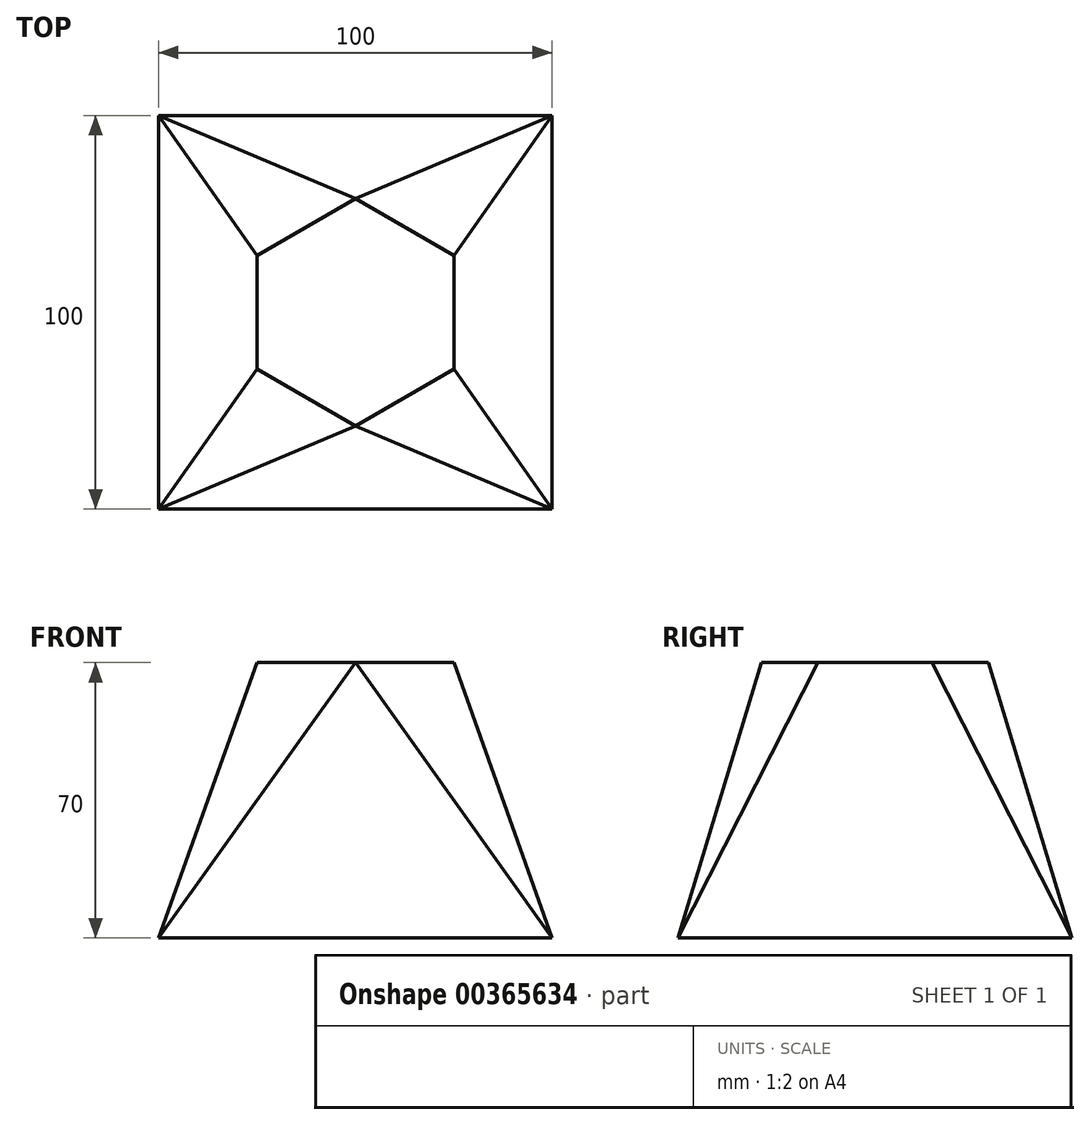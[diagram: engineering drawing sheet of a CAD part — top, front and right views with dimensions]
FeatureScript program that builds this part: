
annotation { "Feature Type Name" : "Feature", "Feature Type Description" : "" }
export const myFeature = defineFeature(function(context is Context, id is Id, definition is map)
    precondition{}
    {
        {
            var Q0;
            Q0=qCreatedBy(makeId("Top.planeOp"),FACE);
            var sketch = newSketch(context, id + "F0", { "sketchPlane" : qUnion([Q0])});
            skLineSegment(sketch, "E0.bottom", {"start": v(50, -50) * mm, "end": v(-50, -50) * mm});
            skLineSegment(sketch, "E0.top", {"start": v(50, 50) * mm, "end": v(-50, 50) * mm});
            skLineSegment(sketch, "E0.left", {"start": v(50, -50) * mm, "end": v(50, 50) * mm});
            skLineSegment(sketch, "E0.right", {"start": v(-50, -50) * mm, "end": v(-50, 50) * mm});
            skPoint(sketch, "E0.middle", {"position": v(0, 0) * mm});
            skSolve(sketch);
        }
        {
            var Q0;
            Q0=qCreatedBy(makeId("Top.planeOp"),FACE);
            cPlane(context, id + "F1", {"entities" : qUnion([Q0]), "cplaneType" : CPlaneType.OFFSET, "offset" : 70 * mm, "width" : 150 * mm, "height" : 150 * mm});
        }
        {
            var Q0;
            Q0=qCreatedBy(id+"F1.planeOp",FACE);
            var sketch = newSketch(context, id + "F2", { "sketchPlane" : qUnion([Q0])});
            skCircle(sketch, "E1.cCircle", {"center": v(0, 0) * mm, "radius": 25 * mm, "construction": true});
            skLineSegment(sketch, "E1.0", {"start": v(-25, -14.43) * mm, "end": v(-25, 14.43) * mm});
            skLineSegment(sketch, "E1.1", {"start": v(-25, 14.43) * mm, "end": v(0, 28.87) * mm});
            skLineSegment(sketch, "E1.2", {"start": v(0, 28.87) * mm, "end": v(25, 14.43) * mm});
            skLineSegment(sketch, "E1.3", {"start": v(25, 14.43) * mm, "end": v(25, -14.43) * mm});
            skLineSegment(sketch, "E1.4", {"start": v(25, -14.43) * mm, "end": v(0, -28.87) * mm});
            skLineSegment(sketch, "E1.5", {"start": v(0, -28.87) * mm, "end": v(-25, -14.43) * mm});
            skPoint(sketch, "E1.0.midPoint", {"position": v(-25, 0) * mm});
            skLineSegment(sketch, "E2", {"start": v(25, 14.43) * mm, "end": v(-25, 14.43) * mm});
            skLineSegment(sketch, "E3", {"start": v(25, -14.43) * mm, "end": v(-25, -14.43) * mm});
            skSolve(sketch);
        }
        {
            var Q0;
            Q0=makeQuery(id+"F2.imprint","IMPRINT",FACE,{"disambiguationData":[TD([[makeQuery(id+"F2.imprint","IMPRINT",EDGE,{"derivedFrom":sQuery(id+"F2.wireOp",EDGE,"E1.0")}),-1.0]])]});
            var Q1;
            Q1=makeQuery(id+"F0.imprint","IMPRINT",FACE,{"disambiguationData":[TD([[makeQuery(id+"F0.imprint","IMPRINT",EDGE,{"derivedFrom":sQuery(id+"F0.wireOp",EDGE,"E0.bottom")}),-1.0]])]});
            loft(context, id + "F3", {"sheetProfilesArray" : [{ "sheetProfileEntities" : qUnion([Q0]) }, { "sheetProfileEntities" : qUnion([Q1]) }]});
        }
        {
            var Q1;
            Q1=makeQuery(id+"F2.imprint","IMPRINT",FACE,{"disambiguationData":[TD([[makeQuery(id+"F2.imprint","IMPRINT",EDGE,{"derivedFrom":sQuery(id+"F2.wireOp",EDGE,"E1.1")}),-1.0]])]});
            var Q2;
            Q2=makeQuery(id+"F3.opLoft","MID_CAP_VERTEX",VERTEX,{"disambiguationData":[OSD([sQuery(id+"F0.wireOp",EDGE,"E0.top"),sQuery(id+"F0.wireOp",EDGE,"E0.left")])],"capPos":1.0});
            loft(context, id + "F4", {"operationType" : NewBodyOperationType.ADD, "sheetProfilesArray" : [{ "sheetProfileEntities" : qUnion([Q1]) }, { "sheetProfileEntities" : qUnion([Q2]) }]});
        }
        {
            var Q1;
            Q1=makeQuery(id+"F2.imprint","IMPRINT",FACE,{"disambiguationData":[TD([[makeQuery(id+"F2.imprint","IMPRINT",EDGE,{"derivedFrom":sQuery(id+"F2.wireOp",EDGE,"E1.1")}),-1.0]])]});
            var Q2;
            Q2=makeQuery(id+"F3.opLoft","MID_CAP_VERTEX",VERTEX,{"disambiguationData":[OSD([sQuery(id+"F0.wireOp",EDGE,"E0.top"),sQuery(id+"F0.wireOp",EDGE,"E0.right")])],"capPos":1.0});
            loft(context, id + "F5", {"operationType" : NewBodyOperationType.ADD, "sheetProfilesArray" : [{ "sheetProfileEntities" : qUnion([Q1]) }, { "sheetProfileEntities" : qUnion([Q2]) }]});
        }
        {
            var Q1;
            Q1=makeQuery(id+"F2.imprint","IMPRINT",FACE,{"disambiguationData":[TD([[makeQuery(id+"F2.imprint","IMPRINT",EDGE,{"derivedFrom":sQuery(id+"F2.wireOp",EDGE,"E1.4")}),-1.0]])]});
            var Q2;
            Q2=makeQuery(id+"F3.opLoft","MID_CAP_VERTEX",VERTEX,{"disambiguationData":[OSD([sQuery(id+"F0.wireOp",EDGE,"E0.bottom"),sQuery(id+"F0.wireOp",EDGE,"E0.right")])],"capPos":1.0});
            loft(context, id + "F6", {"operationType" : NewBodyOperationType.ADD, "sheetProfilesArray" : [{ "sheetProfileEntities" : qUnion([Q1]) }, { "sheetProfileEntities" : qUnion([Q2]) }]});
        }
        {
            var Q1;
            Q1=makeQuery(id+"F2.imprint","IMPRINT",FACE,{"disambiguationData":[TD([[makeQuery(id+"F2.imprint","IMPRINT",EDGE,{"derivedFrom":sQuery(id+"F2.wireOp",EDGE,"E1.4")}),-1.0]])]});
            var Q2;
            Q2=makeQuery(id+"F3.opLoft","MID_CAP_VERTEX",VERTEX,{"disambiguationData":[OSD([sQuery(id+"F0.wireOp",EDGE,"E0.bottom"),sQuery(id+"F0.wireOp",EDGE,"E0.left")])],"capPos":1.0});
            loft(context, id + "F7", {"operationType" : NewBodyOperationType.ADD, "sheetProfilesArray" : [{ "sheetProfileEntities" : qUnion([Q1]) }, { "sheetProfileEntities" : qUnion([Q2]) }]});
        }
        {
            var Q1;
            Q1=makeQuery(id+"F6.opLoft","SWEPT_FACE",FACE,{"disambiguationData":[OSD([sQuery(id+"F2.wireOp",EDGE,"E1.3"),sQuery(id+"F2.wireOp",EDGE,"E1.4"),sQuery(id+"F2.wireOp",EDGE,"E1.5"),sQuery(id+"F2.wireOp",EDGE,"E3")])]});
            var Q2;
            Q2=makeQuery(id+"F7.opLoft","SWEPT_FACE",FACE,{"disambiguationData":[OSD([sQuery(id+"F2.wireOp",EDGE,"E1.0"),sQuery(id+"F2.wireOp",EDGE,"E1.4"),sQuery(id+"F2.wireOp",EDGE,"E1.5"),sQuery(id+"F2.wireOp",EDGE,"E3")])]});
            var Q3;
            Q3=makeQuery(id+"F3.opLoft","MID_CAP_EDGE",EDGE,{"disambiguationData":[OSD([sQuery(id+"F0.wireOp",EDGE,"E0.bottom"),sQuery(id+"F0.wireOp",EDGE,"E0.left"),sQuery(id+"F0.wireOp",EDGE,"E0.right")])],"capPos":1.0});
            loft(context, id + "F8", {"operationType" : NewBodyOperationType.ADD, "addGuides" : true, "sheetProfilesArray" : [{ "sheetProfileEntities" : qUnion([Q1]) }, { "sheetProfileEntities" : qUnion([Q2]) }], "guidesArray" : [{ "guideEntities" : qUnion([Q3]), "guideDerivativeType" : LoftGuideDerivativeType.DEFAULT, "guideDerivativeMagnitude" : 1 }]});
        }
        {
            var Q1;
            Q1=makeQuery(id+"F4.opLoft","SWEPT_FACE",FACE,{"disambiguationData":[OSD([sQuery(id+"F2.wireOp",EDGE,"E1.0"),sQuery(id+"F2.wireOp",EDGE,"E1.1"),sQuery(id+"F2.wireOp",EDGE,"E1.2"),sQuery(id+"F2.wireOp",EDGE,"E2")])]});
            var Q2;
            Q2=makeQuery(id+"F5.opLoft","SWEPT_FACE",FACE,{"disambiguationData":[OSD([sQuery(id+"F2.wireOp",EDGE,"E1.1"),sQuery(id+"F2.wireOp",EDGE,"E1.2"),sQuery(id+"F2.wireOp",EDGE,"E1.3"),sQuery(id+"F2.wireOp",EDGE,"E2")])]});
            var Q3;
            Q3=makeQuery(id+"F3.opLoft","MID_CAP_EDGE",EDGE,{"disambiguationData":[OSD([sQuery(id+"F0.wireOp",EDGE,"E0.top"),sQuery(id+"F0.wireOp",EDGE,"E0.left"),sQuery(id+"F0.wireOp",EDGE,"E0.right")])],"capPos":1.0});
            loft(context, id + "F9", {"operationType" : NewBodyOperationType.ADD, "addGuides" : true, "sheetProfilesArray" : [{ "sheetProfileEntities" : qUnion([Q1]) }, { "sheetProfileEntities" : qUnion([Q2]) }], "guidesArray" : [{ "guideEntities" : qUnion([Q3]), "guideDerivativeType" : LoftGuideDerivativeType.DEFAULT, "guideDerivativeMagnitude" : 1 }]});
        }
    });
